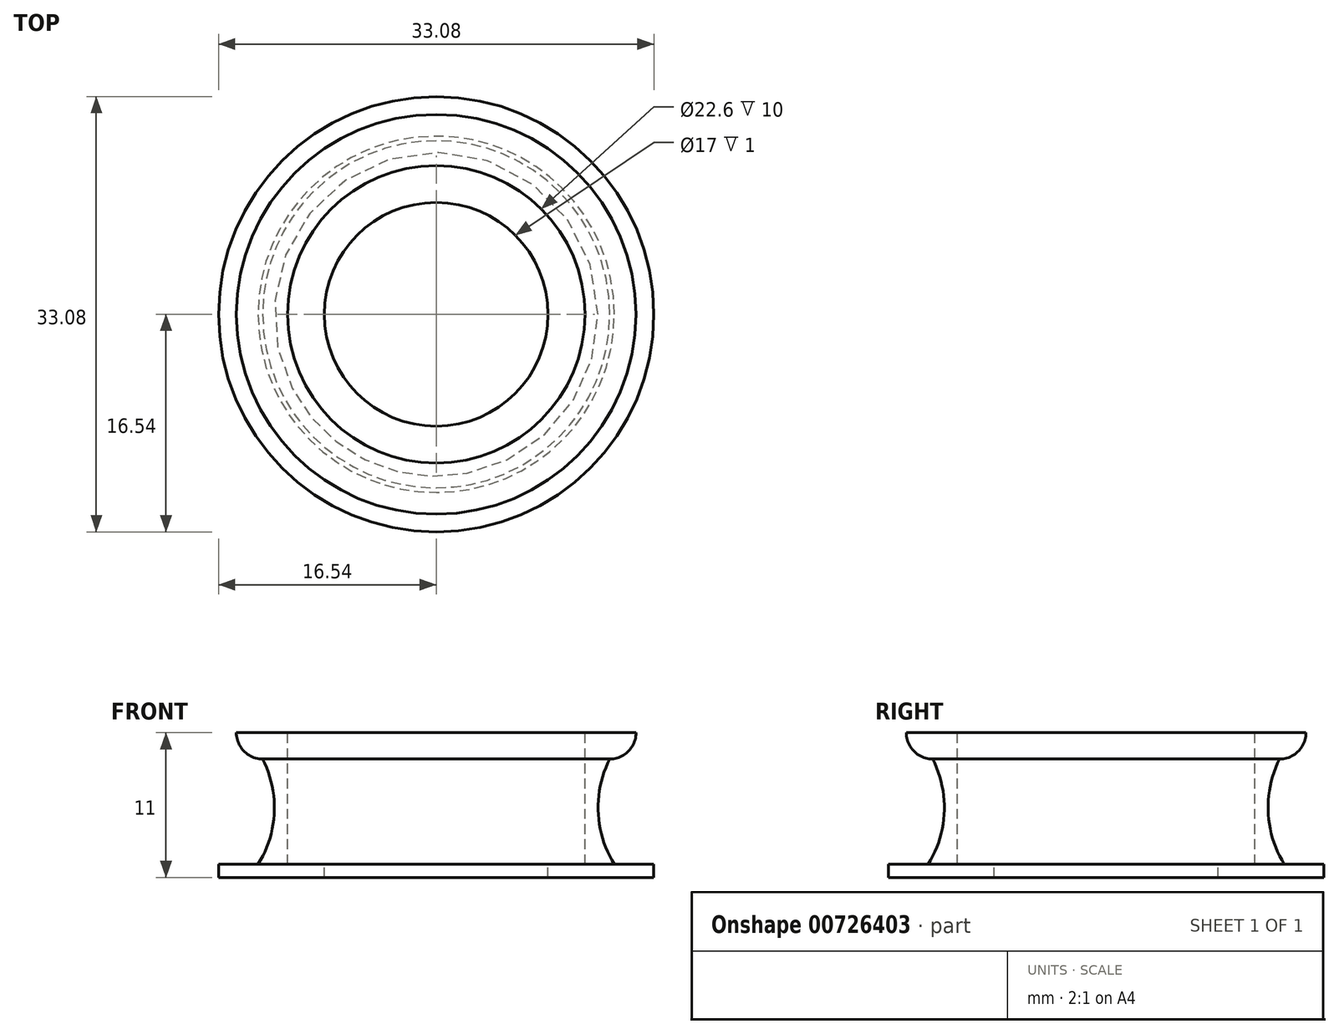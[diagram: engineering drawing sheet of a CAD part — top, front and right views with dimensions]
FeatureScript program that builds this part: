
annotation { "Feature Type Name" : "Feature", "Feature Type Description" : "" }
export const myFeature = defineFeature(function(context is Context, id is Id, definition is map)
    precondition{}
    {
        {
            var Q0;
            Q0=qCreatedBy(makeId("Front.planeOp"),FACE);
            var sketch = newSketch(context, id + "F0", { "sketchPlane" : qUnion([Q0])});
            skArc(sketch, "E0", {"start": v(13.19, 4) * mm, "mid": v(12.3, -0.05) * mm, "end": v(13.54, -4) * mm});
            skLineSegment(sketch, "E1", {"start": v(11.3, 4) * mm, "end": v(11.3, -4) * mm});
            skLineSegment(sketch, "E2", {"start": v(13.19, 4) * mm, "end": v(11.3, 4) * mm});
            skLineSegment(sketch, "E3", {"start": v(13.54, -4) * mm, "end": v(11.3, -4) * mm});
            skLineSegment(sketch, "E4", {"start": v(0, 16.82) * mm, "end": v(0, -19.15) * mm, "construction": true});
            skSolve(sketch);
        }
        {
            var Q0;
            Q0=makeQuery(id+"F0.imprint","IMPRINT",FACE,{"disambiguationData":[TD([[makeQuery(id+"F0.imprint","IMPRINT",EDGE,{"derivedFrom":sQuery(id+"F0.wireOp",EDGE,"E0")}),-1.0]])]});
            var Q1;
            Q1=sQuery(id+"F0.wireOp",EDGE,"E4");
            revolve(context, id + "F1", {"surfaceOperationType" : NewSurfaceOperationType.NEW, "entities" : qUnion([Q0]), "axis" : qUnion([Q1]), "revolveType" : RevolveType.FULL});
        }
        {
            var Q0;
            Q0=makeQuery(id+"F1.opRevolve","SWEPT_FACE",FACE,{"disambiguationData":[OSD([sQuery(id+"F0.wireOp",EDGE,"E3")])]});
            var sketch = newSketch(context, id + "F2", { "sketchPlane" : qUnion([Q0])});
            skCircle(sketch, "E5.0", {"center": v(0, 0) * mm, "radius": 16.54 * mm});
            skCircle(sketch, "E6", {"center": v(0, 0) * mm, "radius": 8.5 * mm});
            skSolve(sketch);
        }
        {
            var Q0;
            Q0 = qSketchRegion(id + "F2", true);
            extrude(context, id + "F3", {"entities" : qUnion([Q0]), "operationType" : NewBodyOperationType.ADD, "depth" : 1 * mm, "offsetDistance" : 25 * mm});
        }
        {
            var Q0;
            Q0=makeQuery(id+"F1.opRevolve","SWEPT_FACE",FACE,{"disambiguationData":[OSD([sQuery(id+"F0.wireOp",EDGE,"E2")])]});
            var sketch = newSketch(context, id + "F4", { "sketchPlane" : qUnion([Q0])});
            skCircle(sketch, "E7.0", {"center": v(0, 0) * mm, "radius": 15.19 * mm});
            skCircle(sketch, "E8.0", {"center": v(0, 0) * mm, "radius": 11.3 * mm});
            skSolve(sketch);
        }
        {
            var Q0;
            Q0 = qSketchRegion(id + "F4", true);
            extrude(context, id + "F5", {"entities" : qUnion([Q0]), "operationType" : NewBodyOperationType.ADD, "depth" : 2 * mm, "offsetDistance" : 25 * mm});
        }
        {
            var Q0;
            Q0=makeQuery(id+"F5.opExtrude","CAP_EDGE",EDGE,{"disambiguationData":[OSD([sQuery(id+"F4.wireOp",EDGE,"E7.0")])],"isStart":true});
            fillet(context, id + "F6", {"entities" : qUnion([Q0]), "radius" : 2 * mm, "tangentPropagation" : true, "allowEdgeOverflow" : false});
        }
    });
